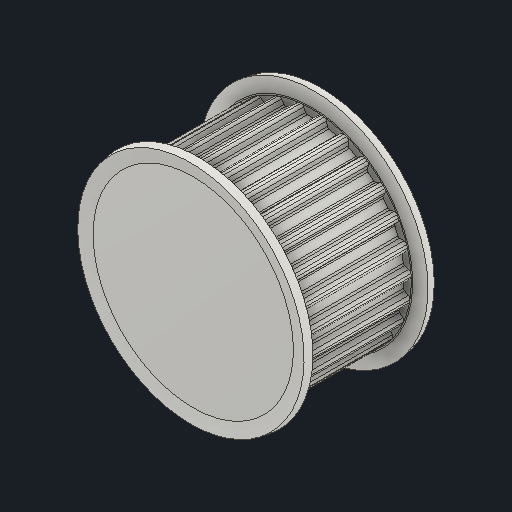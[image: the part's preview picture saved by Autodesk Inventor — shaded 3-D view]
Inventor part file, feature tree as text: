
AUTODESK INVENTOR PART (.ipt)
format: ipt  version: 2023.1 (Build 271208000, 208)  size: 437,248 bytes
history: native  units: mm (DEFAULTED — no unit token found)
features: other x3, extrude x2, fillet x1, pattern_circular x1
ambient origin geometry x8: Origin, YZ Plane, XZ Plane, XY Plane, X Axis, Y Axis, Z Axis, Center Point
bodies: Solid1 (feature_tree)
feature tree (7):
  other  "Pulley Sketch"
  extrude  "Base Body"  Depth=21.485917mm
  extrude  "Tooth"  Depth=0.3mm
  fillet  "Tooth Fillet"  Radius=0.75mm
  pattern_circular  "Teeth"  [2 undecoded]
  other  "Left flange"
  other  "Right flange"
note: 2 required parameter values undecoded (feature->parameter linkage not recoverable at this tier; creation-order binding heuristic only, values carry confidence <= 0.55)
